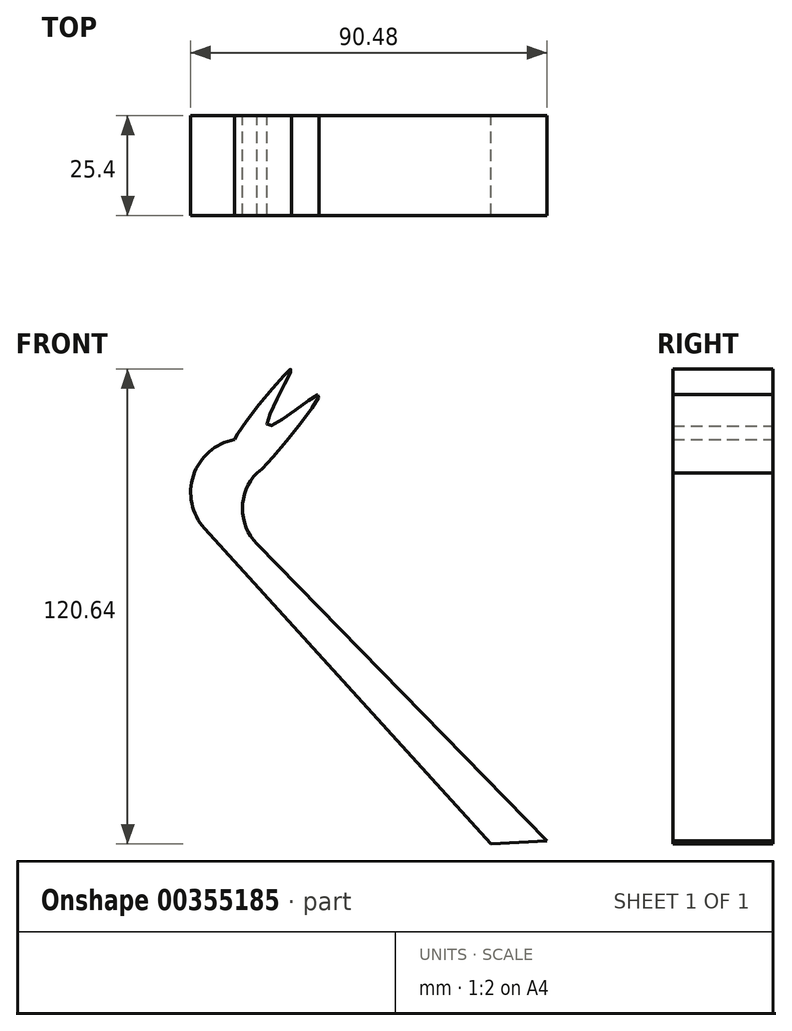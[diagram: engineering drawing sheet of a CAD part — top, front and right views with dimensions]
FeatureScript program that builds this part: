
annotation { "Feature Type Name" : "Feature", "Feature Type Description" : "" }
export const myFeature = defineFeature(function(context is Context, id is Id, definition is map)
    precondition{}
    {
        {
            var Q0;
            Q0=qCreatedBy(makeId("Front.planeOp"),FACE);
            var sketch = newSketch(context, id + "F0", { "sketchPlane" : qUnion([Q0])});
            skLineSegment(sketch, "E0", {"start": v(48.09, -76.2) * mm, "end": v(-24.72, 3.94) * mm});
            skLineSegment(sketch, "E1", {"start": v(62.22, -75.4) * mm, "end": v(-11.41, 0) * mm});
            skArc(sketch, "E2", {"start": v(-17.12, 26.49) * mm, "mid": v(-27.55, 17.45) * mm, "end": v(-24.72, 3.94) * mm});
            skArc(sketch, "E3", {"start": v(-11.41, 18.06) * mm, "mid": v(-15.09, 9.03) * mm, "end": v(-11.41, 0) * mm});
            skFitSpline(sketch, "E4", {"points": [v(-17.12, 26.49) * mm, v(-9.5, 31.92) * mm, v(-11.41, 24.04) * mm, v(-5.16, 29.2) * mm, v(-11.41, 18.06) * mm, v(4.35, 37.9) * mm, v(-8.7, 30.02) * mm, v(-2.72, 44.42) * mm, v(-17.12, 26.49) * mm]});
            skLineSegment(sketch, "E5", {"start": v(62.22, -75.4) * mm, "end": v(48.09, -76.2) * mm});
            skSolve(sketch);
        }
        {
            var Q0;
            Q0 = qSketchRegion(id + "F0", true);
            extrude(context, id + "F1", {"entities" : qUnion([Q0]), "depth" : 25.4 * mm});
        }
    });
